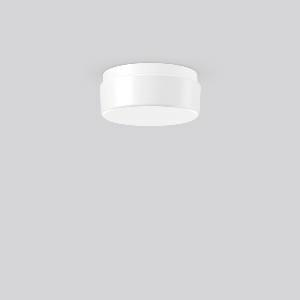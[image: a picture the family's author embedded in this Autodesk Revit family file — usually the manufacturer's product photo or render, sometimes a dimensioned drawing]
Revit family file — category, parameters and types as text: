
# Revit family: kreis_211416_002_1_b86c
name_source: partatom
category: Lighting Fixtures
units: mm (PartAtom-declared; Revit-internal decimal feet)

## family parameters
Cut with Voids When Loaded = No
Host = Face
Light Source = No
Part Type = Normal
Room Calculation Point = No
Round Connector Dimension = Use Diameter
Shared = No

## types (1)
- KREIS (1 x LED Modul 840, 1200 lm, 4000)
    Apparent Load = 11 VA
    CIE Flux Codes = 38 68 88 79 100
    Color Rendering = 80
    Color Temperature = 4000
    Default Elevation = 1800 mm
    Description = Series: KREIS
Round surface-mounted luminaire in classic design. Base: plastic. Opal glass: mouth-blown, satin finish. Diffuser fastening: spring system. Suitable for Ceiling mounting, Wall (surface). IP 43 ceiling mounting, IP 44 wall mounting. 
Colour: white
Diameter: 280 mm
Height: 120 mm
Lamp: LED exchangeable
Socket: without socket
Colour temperature: 4000K
Colour rendering index (CRI): 80
System power: 11 W
Rated luminous flux: 1200 lm
Luminous efficiency: 109 lm/W
Control gear: AC Strom, dim.Ph.an-/abschnitt
Protection class: I
Type of protection: IP 43
    Height = 120 mm
    Lamp = 1 x LED Modul 840
    Lamp Light Flux = 1200 lm
    Lamp count = 1
    Length = 280 mm
    Lifetime = 50000 h
    Luminous efficacy = 109 lm/W
    Manufacturer = RZB
    ModVariant = No
    Model = 211416.002.1
    Mounting Place = Ceiling, Wall
    Mounting Type = Surface mounted
    Number of Poles = 1
    OnlyDefault = Yes
    Power Factor = 1
    Product Name = KREIS
    Product group = Surface mounted ceiling and wall luminaires
    ProductGroupID = 305
    Protection Class = Protection class I
    Protection Degree = IP 43
    RLX_Detail_Level = 1
    RLX_Emergency_Light_Flux = 0 lm
    RLX_Emergency_Type = 0
    RLX_Emergency_Type_DB = No
    RlxData = <blob elided: 11665 chars, md5=4f294fc1>
    Socket = socket
    Standby Power = 0 W
    System Light Flux = 1200 lm
    System Power = 11 W
    Type Comments = Product without accessories
    Type Image = 21171.002.jpg
    URL = http://relux.com
    VarID = ---
    Voltage = 230 V
    Voltage Range = 220-240 V
    Weight = 0.00 kg
    Width = 0 mm  [stored 0 ft]

note: [stored X ft] marks values corroborated as IEEE doubles in the binary element streams (Revit-internal decimal feet)

## geometry (parser evidence)
native form markers: Sweep x12
no freeform markers — native parametric forms only
